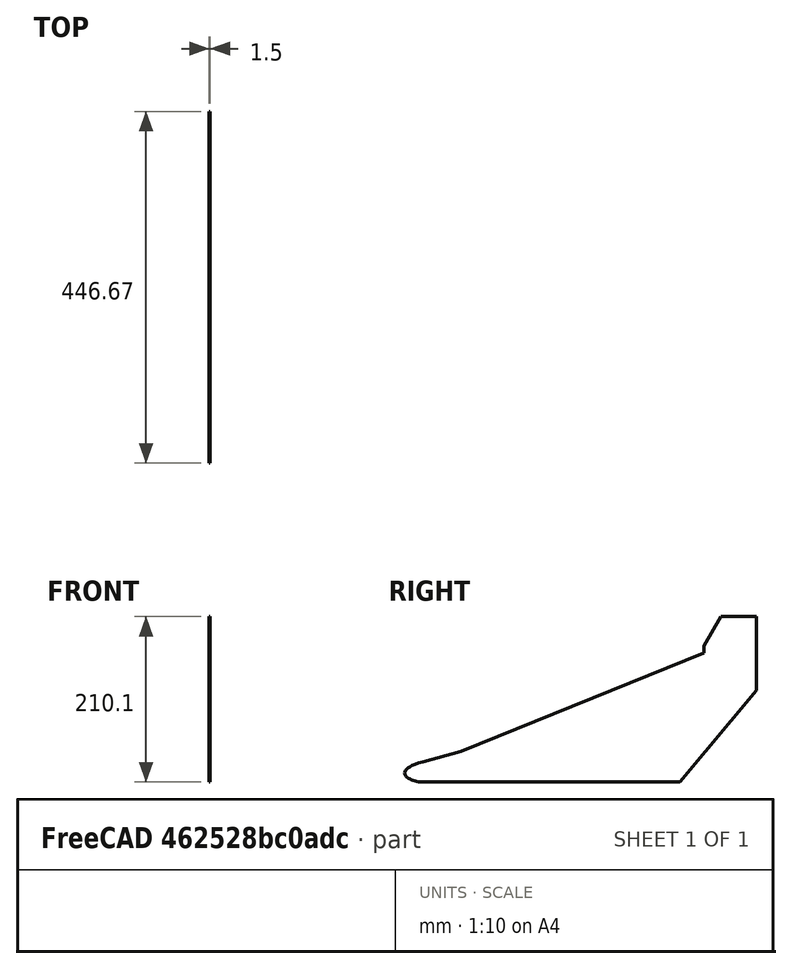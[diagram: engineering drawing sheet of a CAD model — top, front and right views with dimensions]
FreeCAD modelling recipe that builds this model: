
FCSTD DOCUMENT  (FreeCAD 0.18R16146 (Git))
Label: SeitenteilInnen
License: All rights reserved
LicenseURL: http://en.wikipedia.org/wiki/All_rights_reserved
objects: PartDesign::Body×2, Sketcher::SketchObject×1, PartDesign::Pad×1
note: 5 computed .brp shape members not serialized (recipe doc carries the construction recipe); baked Part::Feature solids carry a one-line shape summary decoded from their .brp

FEATURE [Sketcher::SketchObject] CopySketch003
  Placement = pos=(0,0,0) rot=(0.57735,0.57735,0.57735;2.0944rad)
  sketch-geometry (15):
    g0: LineSegment StartX=-225 StartY=0 StartZ=0 EndX=100 EndY=0 EndZ=0
    g1: LineSegment StartX=100 StartY=0 StartZ=0 EndX=197.336 EndY=116 EndZ=0
    g2: LineSegment StartX=197.336 StartY=116 StartZ=0 EndX=197.336 EndY=210 EndZ=0
    g3: LineSegment StartX=197.336 StartY=210 StartZ=0 EndX=152.336 EndY=210 EndZ=0
    g4-g7: Circle [constr] x4 (B-spline internal-alignment scaffolding for g8; pole/knot coordinates omitted)
    g8: BSplineCurve PolesCount=4 KnotsCount=2 Degree=3 IsPeriodic=0
    g9: GeomPoint [constr] X=-225 Y=0 Z=0
    g10: GeomPoint [constr] X=-226.199 Y=25.5886 Z=0
    g11: LineSegment StartX=130.836 StartY=163.99 StartZ=0 EndX=130.836 EndY=172.761 EndZ=0
    g12: LineSegment StartX=130.836 StartY=172.761 StartZ=0 EndX=152.336 EndY=210 EndZ=0
    g13: LineSegment StartX=130.836 StartY=163.99 StartZ=0 EndX=-177.903 EndY=38.5296 EndZ=0
    g14: LineSegment StartX=-177.903 StartY=38.5296 StartZ=0 EndX=-226.199 EndY=25.5886 EndZ=0
  constraints (37):
    c: Horizontal(g0)
    c: Coincident(g0,g1)
    c: Coincident(g1,g2)
    c: Vertical(g2)
    c: Coincident(g2,g3)
    c: Horizontal(g3)
    c: Coincident(g8,g0)
    c: Radius(g4) = 3
    c: Equal(g4,g5)
    c: Equal(g4,g6)
    c: Equal(g4,g7)
    c: InternalAlignment(g4-g7 -> g8) x4
    c: InternalAlignment(g9,g8)
    c: InternalAlignment(g10,g8)
    c: DistanceX(g0,g8) = -1.19908
    c: DistanceY(g0,g8) = 25.5886
    c: DistanceX(g5,g8) = 14.8153
    c: DistanceY(g5,g8) = 27.0505
    c: DistanceX(g6,g8) = 43.8227
    c: DistanceY(g6,g8) = 11.8456
    c: Angle(g1,g-1) = 2.26893
    c: DistanceY(g-1,g2) = 210
    c: PointOnObject(g-1,g0)
    c: DistanceX(g3,g3) = 45
    c: DistanceX(g-1,g0) = 100
    c: Vertical(g11)
    c: Coincident(g11,g12)
    c: Coincident(g12,g3)
    c: Distance(g12) = 43
    c: Angle(g12,g-1) = 2.0944
    c: DistanceY(g2,g2) = 94
    c: Coincident(g11,g13)
    c: Coincident(g13,g14)
    c: Coincident(g14,g8)
    c: Angle(g0,g14) = 0.261799
    c: Distance(g14) = 50
    c: DistanceX(g0,g0) = 325
FEATURE [PartDesign::Pad] Pad
  Length = 1.5
  Length2 = 100
  Placement = pos=(0,0,0) rot=(0.57735,0.57735,0.57735;2.0944rad)
  Profile = -> CopySketch003
  Type = 0
FEATURE [PartDesign::Body] Body002  label="Seitenteil_innen"
  Group = -> [Pad]
  Origin = -> Origin133
  Tip = -> Pad
FEATURE [PartDesign::Body] Body
  Origin = -> Origin
